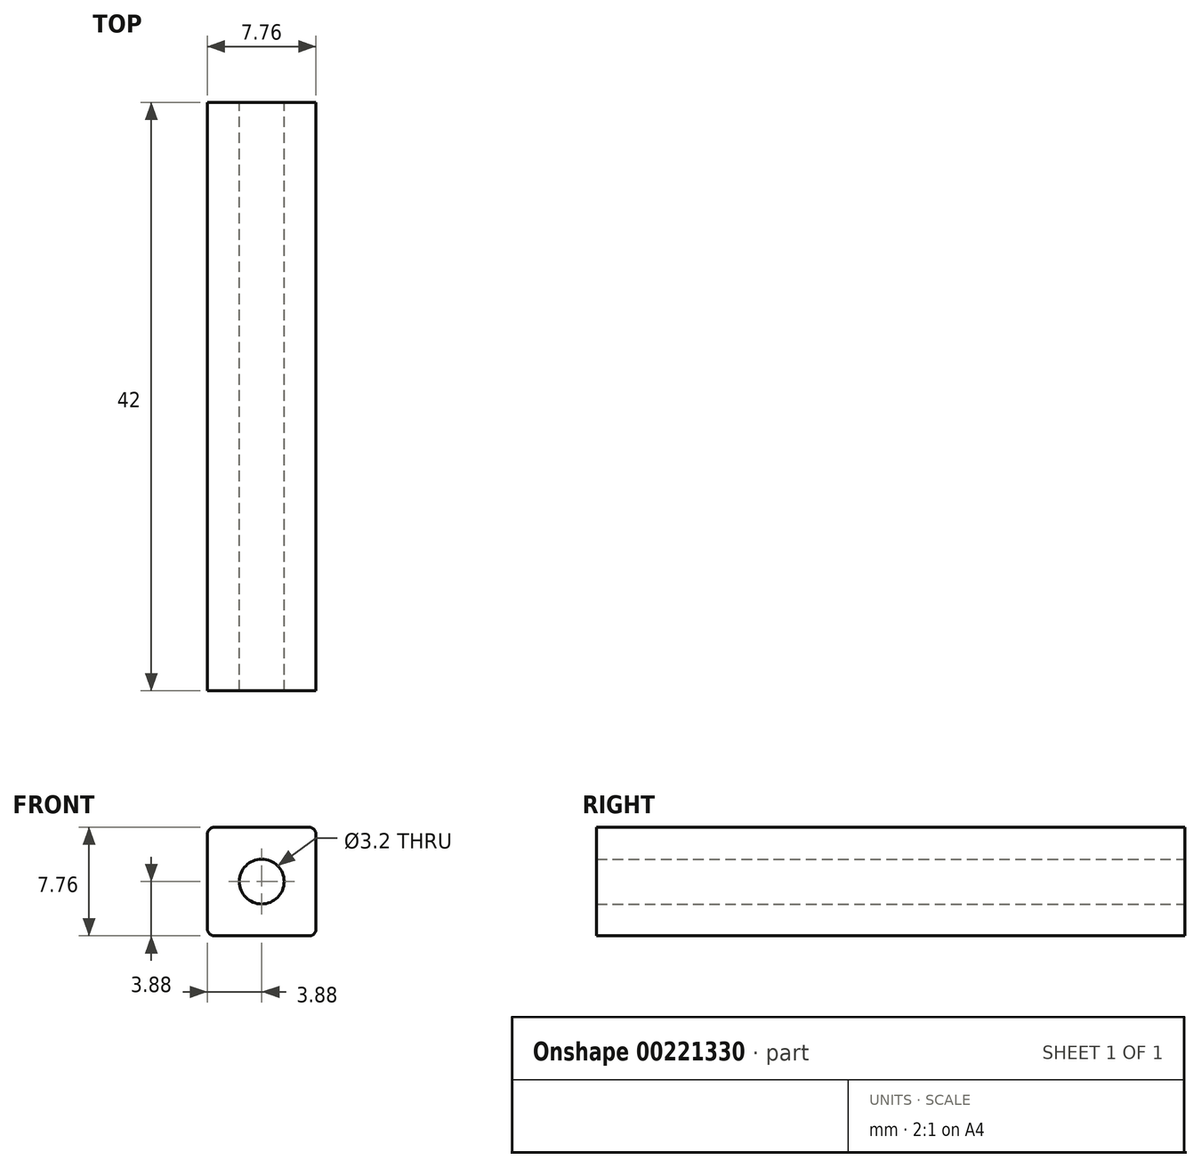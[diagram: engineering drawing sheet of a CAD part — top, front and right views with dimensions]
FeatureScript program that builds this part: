
annotation { "Feature Type Name" : "Feature", "Feature Type Description" : "" }
export const myFeature = defineFeature(function(context is Context, id is Id, definition is map)
    precondition{}
    {
        {
            var Q0;
            Q0=qCreatedBy(makeId("Front.planeOp"),FACE);
            var sketch = newSketch(context, id + "F0", { "sketchPlane" : qUnion([Q0])});
            skCircle(sketch, "E0", {"center": v(0, 0) * mm, "radius": 1.6 * mm});
            skLineSegment(sketch, "E1.bottom", {"start": v(3.87, -3.88) * mm, "end": v(-3.88, -3.88) * mm});
            skLineSegment(sketch, "E1.top", {"start": v(3.88, 3.88) * mm, "end": v(-3.87, 3.88) * mm});
            skLineSegment(sketch, "E1.left", {"start": v(3.87, -3.88) * mm, "end": v(3.88, 3.88) * mm});
            skLineSegment(sketch, "E1.right", {"start": v(-3.88, -3.88) * mm, "end": v(-3.87, 3.88) * mm});
            skSolve(sketch);
        }
        {
            var Q0;
            Q0=makeQuery(id+"F0.imprint","IMPRINT",FACE,{"disambiguationData":[TD([[makeQuery(id+"F0.imprint","IMPRINT",EDGE,{"derivedFrom":sQuery(id+"F0.wireOp",EDGE,"E0")}),-1.0]])]});
            extrude(context, id + "F1", {"entities" : qUnion([Q0]), "depth" : 42 * mm});
        }
        {
            var Q0;
            Q0=makeQuery(id+"F1.opExtrude","SWEPT_EDGE",EDGE,{"disambiguationData":[OSD([sQuery(id+"F0.wireOp",EDGE,"E1.top"),sQuery(id+"F0.wireOp",EDGE,"E1.right")])]});
            var Q1;
            Q1=makeQuery(id+"F1.opExtrude","SWEPT_EDGE",EDGE,{"disambiguationData":[OSD([sQuery(id+"F0.wireOp",EDGE,"E1.top"),sQuery(id+"F0.wireOp",EDGE,"E1.left")])]});
            var Q2;
            Q2=makeQuery(id+"F1.opExtrude","SWEPT_EDGE",EDGE,{"disambiguationData":[OSD([sQuery(id+"F0.wireOp",EDGE,"E1.bottom"),sQuery(id+"F0.wireOp",EDGE,"E1.left")])]});
            var Q3;
            Q3=makeQuery(id+"F1.opExtrude","SWEPT_EDGE",EDGE,{"disambiguationData":[OSD([sQuery(id+"F0.wireOp",EDGE,"E1.bottom"),sQuery(id+"F0.wireOp",EDGE,"E1.right")])]});
            fillet(context, id + "F2", {"entities" : qUnion([Q0, Q1, Q2, Q3]), "radius" : 0.5 * mm, "tangentPropagation" : true, "allowEdgeOverflow" : false});
        }
    });
